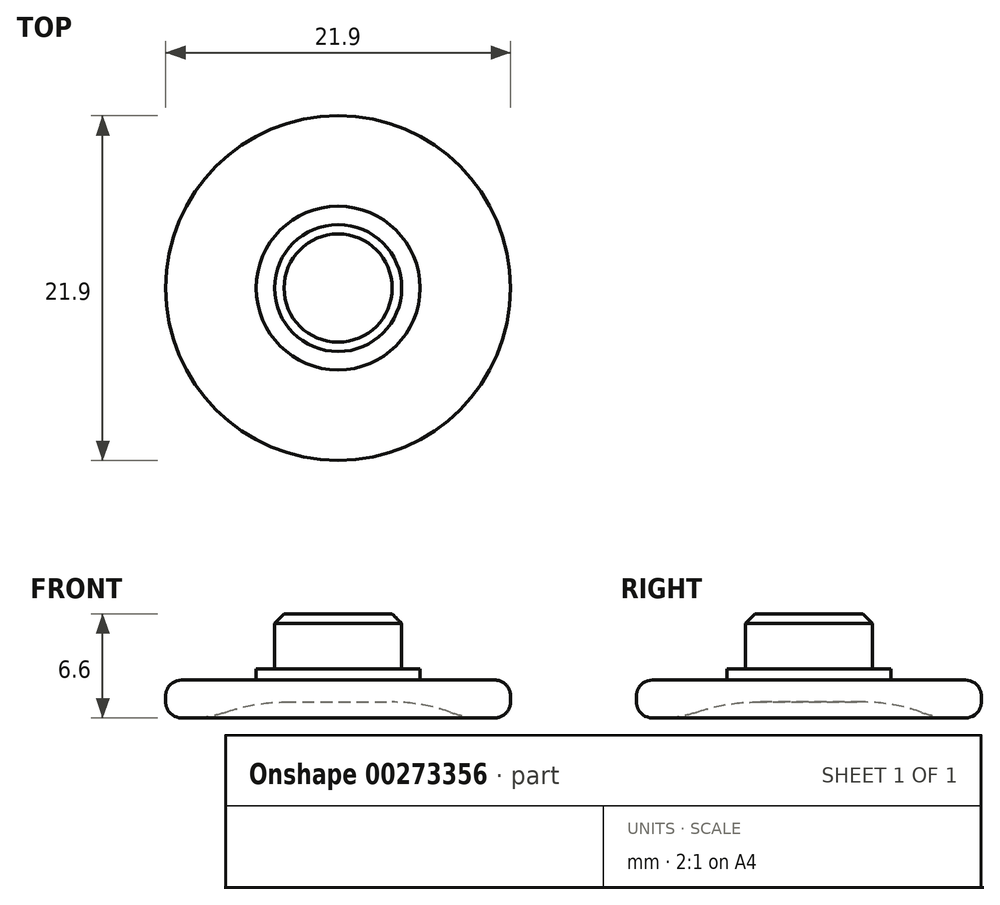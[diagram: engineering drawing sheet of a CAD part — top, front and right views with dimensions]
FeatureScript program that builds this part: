
annotation { "Feature Type Name" : "Feature", "Feature Type Description" : "" }
export const myFeature = defineFeature(function(context is Context, id is Id, definition is map)
    precondition{}
    {
        {
            var Q0;
            Q0=qCreatedBy(makeId("Top.planeOp"),FACE);
            var sketch = newSketch(context, id + "F0", { "sketchPlane" : qUnion([Q0])});
            skCircle(sketch, "E0", {"center": v(0, 0) * mm, "radius": 10.95 * mm});
            skSolve(sketch);
        }
        {
            var Q0;
            Q0=makeQuery(id+"F0.imprint","IMPRINT",FACE,{"disambiguationData":[TD([[makeQuery(id+"F0.imprint","IMPRINT",EDGE,{"derivedFrom":sQuery(id+"F0.wireOp",EDGE,"E0")}),1.0]])]});
            extrude(context, id + "F1", {"entities" : qUnion([Q0]), "depth" : 2.4 * mm});
        }
        {
            var Q0;
            Q0=makeQuery(id+"F1.opExtrude","CAP_FACE",FACE,{"disambiguationData":[OSD([sQuery(id+"F0.wireOp",EDGE,"E0")])],"isStart":false});
            var sketch = newSketch(context, id + "F2", { "sketchPlane" : qUnion([Q0])});
            skCircle(sketch, "E1", {"center": v(0, 0) * mm, "radius": 4.04 * mm});
            skSolve(sketch);
        }
        {
            var Q0;
            Q0=makeQuery(id+"F2.imprint","IMPRINT",FACE,{"disambiguationData":[TD([[makeQuery(id+"F2.imprint","IMPRINT",EDGE,{"derivedFrom":sQuery(id+"F2.wireOp",EDGE,"E1")}),1.0]])]});
            extrude(context, id + "F3", {"entities" : qUnion([Q0]), "operationType" : NewBodyOperationType.ADD, "depth" : 4.2 * mm});
        }
        {
            var Q0;
            Q0=makeQuery(id+"F1.opExtrude","CAP_EDGE",EDGE,{"disambiguationData":[OSD([sQuery(id+"F0.wireOp",EDGE,"E0")])],"isStart":false});
            fillet(context, id + "F4", {"entities" : qUnion([Q0]), "radius" : 1 * mm, "tangentPropagation" : true, "allowEdgeOverflow" : false});
        }
        {
            var Q0;
            Q0=makeQuery(id+"F1.opExtrude","CAP_FACE",FACE,{"disambiguationData":[OSD([sQuery(id+"F0.wireOp",EDGE,"E0")])],"isStart":false});
            var sketch = newSketch(context, id + "F5", { "sketchPlane" : qUnion([Q0])});
            skCircle(sketch, "E2", {"center": v(0, 0) * mm, "radius": 5.2 * mm});
            skSolve(sketch);
        }
        {
            var Q0;
            Q0=makeQuery(id+"F5.imprint","IMPRINT",FACE,{"disambiguationData":[TD([[makeQuery(id+"F5.imprint","IMPRINT",EDGE,{"derivedFrom":sQuery(id+"F5.wireOp",EDGE,"E2")}),1.0]])]});
            extrude(context, id + "F6", {"entities" : qUnion([Q0]), "operationType" : NewBodyOperationType.ADD, "depth" : .7 * mm});
        }
        {
            var Q0;
            Q0=makeQuery(id+"F1.opExtrude","CAP_EDGE",EDGE,{"disambiguationData":[OSD([sQuery(id+"F0.wireOp",EDGE,"E0")])],"isStart":true});
            fillet(context, id + "F7", {"entities" : qUnion([Q0]), "radius" : 1 * mm, "tangentPropagation" : true, "allowEdgeOverflow" : false});
        }
        {
            var Q0;
            Q0=makeQuery(id+"F1.opExtrude","CAP_FACE",FACE,{"disambiguationData":[OSD([sQuery(id+"F0.wireOp",EDGE,"E0")])],"isStart":true});
            var sketch = newSketch(context, id + "F8", { "sketchPlane" : qUnion([Q0])});
            skCircle(sketch, "E3", {"center": v(0, 0) * mm, "radius": 8 * mm});
            skSolve(sketch);
        }
        {
            var Q0;
            Q0=makeQuery(id+"F8.imprint","IMPRINT",FACE,{"disambiguationData":[TD([[makeQuery(id+"F8.imprint","IMPRINT",EDGE,{"derivedFrom":sQuery(id+"F8.wireOp",EDGE,"E3")}),1.0]])]});
            extrude(context, id + "F9", {"entities" : qUnion([Q0]), "operationType" : NewBodyOperationType.REMOVE, "oppositeDirection" : true, "depth" : 1 * mm});
        }
        {
            var Q0;
            Q0=makeQuery(id+"F9.boolean.opBoolean","COPY",EDGE,{"derivedFrom":makeQuery(id+"F9.opExtrude","CAP_EDGE",EDGE,{"disambiguationData":[OSD([sQuery(id+"F8.wireOp",EDGE,"E3")])],"isStart":false})});
            fillet(context, id + "F10", {"entities" : qUnion([Q0]), "radius" : 11 * mm, "tangentPropagation" : true, "allowEdgeOverflow" : false});
        }
        {
            var Q0;
            Q0=makeQuery(id+"F3.opExtrude","CAP_EDGE",EDGE,{"disambiguationData":[OSD([sQuery(id+"F2.wireOp",EDGE,"E1")])],"isStart":false});
            chamfer(context, id + "F11", {"entities" : qUnion([Q0]), "width" : .6 * mm, "tangentPropagation" : true});
        }
        {
            var Q0;
            Q0=makeQuery(id+"F10.opFillet","BLEND_EDGE",EDGE,{"blendedFrom":[makeQuery(id+"F9.boolean.opBoolean","COPY",EDGE,{"derivedFrom":makeQuery(id+"F9.opExtrude","CAP_EDGE",EDGE,{"disambiguationData":[OSD([sQuery(id+"F8.wireOp",EDGE,"E3")])],"isStart":false})}),makeQuery(id+"F1.opExtrude","CAP_FACE",FACE,{"disambiguationData":[OSD([sQuery(id+"F0.wireOp",EDGE,"E0")])],"isStart":true})],"blendedInto":[makeQuery(id+"F1.opExtrude","CAP_FACE",FACE,{"disambiguationData":[OSD([sQuery(id+"F0.wireOp",EDGE,"E0")])],"isStart":true})]});
            fillet(context, id + "F12", {"entities" : qUnion([Q0]), "radius" : 6 * mm, "tangentPropagation" : true, "allowEdgeOverflow" : false});
        }
    });
